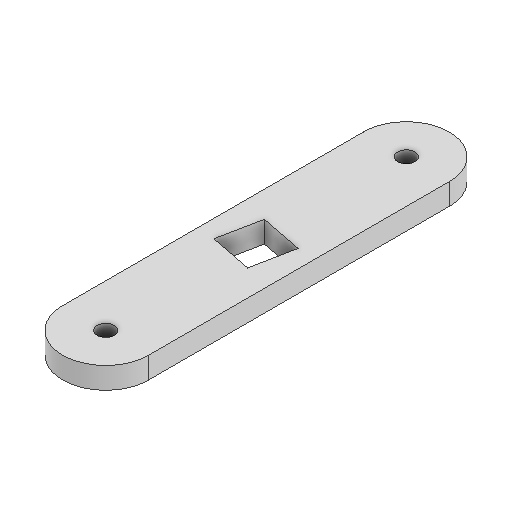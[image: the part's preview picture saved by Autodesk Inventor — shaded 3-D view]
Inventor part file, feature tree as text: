
AUTODESK INVENTOR PART (.ipt)
format: ipt  version: 2025.2 (Build 292293000, 293)  size: 100,352 bytes
history: native  units: mm
features: extrude x1, sketch x1
ambient origin geometry x8: Origin, YZ Plane, XZ Plane, XY Plane, X Axis, Y Axis, Z Axis, Center Point
bodies: Solid1 (feature_tree)
feature tree (2):
  extrude  "Extrusion1"  Depth=20.0mm
  sketch  "Sketch1"  dims[d0=35.0mm d1=20.0mm d2=4.0mm d3=4.0mm d4=10.0mm d5=13.744468mm d6=10.0mm d7=5.0mm d8=0.0mm]
